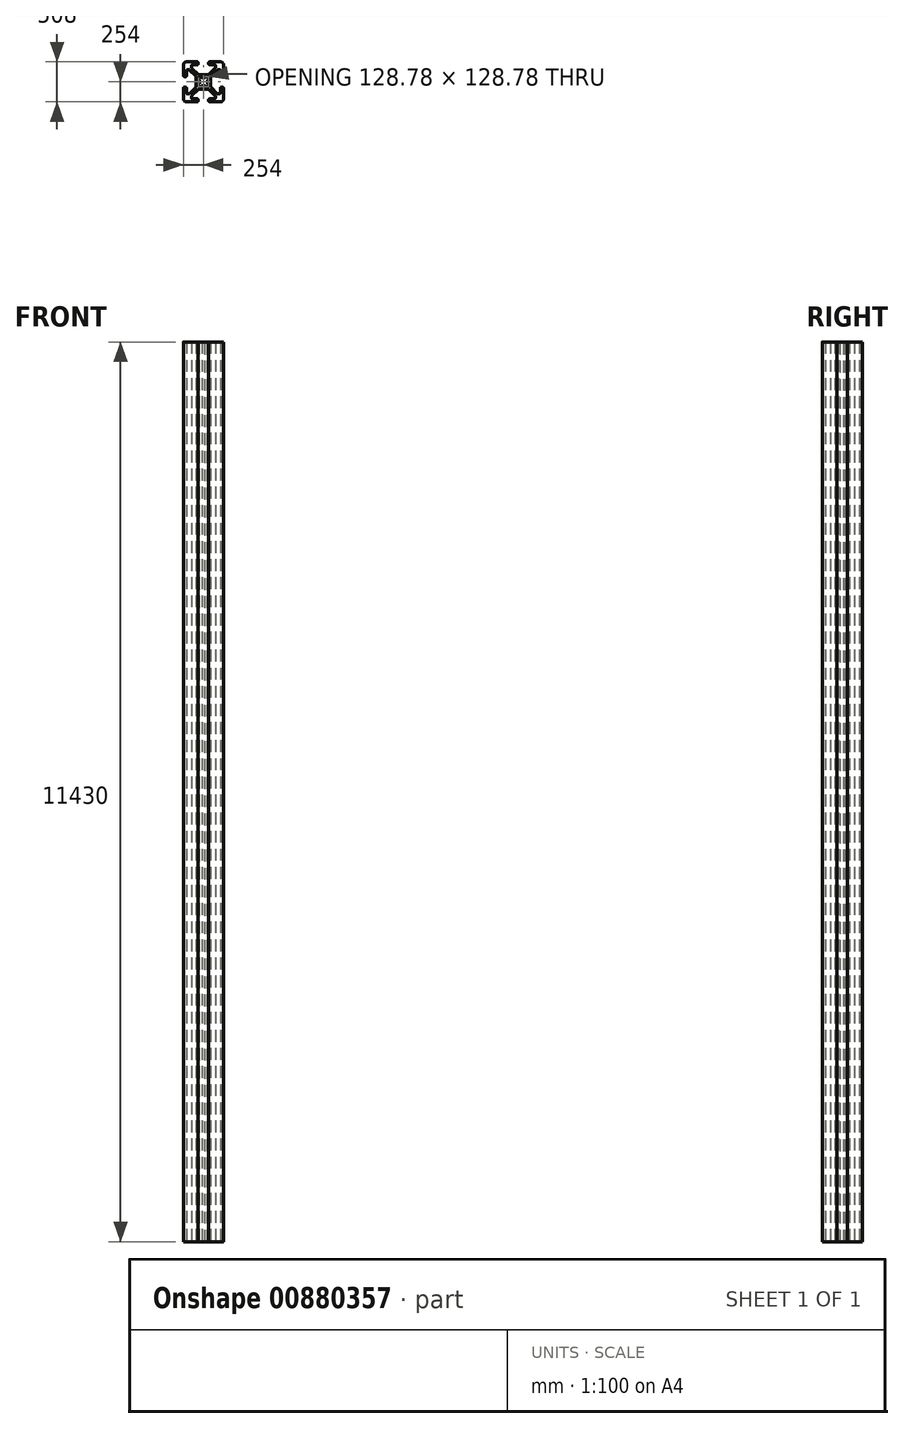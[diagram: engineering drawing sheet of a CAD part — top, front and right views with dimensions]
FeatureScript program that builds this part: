
annotation { "Feature Type Name" : "Feature", "Feature Type Description" : "" }
export const myFeature = defineFeature(function(context is Context, id is Id, definition is map)
    precondition{}
    {
        {
            var Q0;
            Q0=qCreatedBy(makeId("Top.planeOp"),FACE);
            var sketch = newSketch(context, id + "F0", { "sketchPlane" : qUnion([Q0])});
            skArc(sketch, "E0", {"start": v(-53.97, -58.53) * mm, "mid": v(-34.45, -63.65) * mm, "end": v(-20.42, -49.15) * mm});
            skLineSegment(sketch, "E1", {"start": v(-58.53, -53.97) * mm, "end": v(-53.97, -58.53) * mm});
            skArc(sketch, "E2", {"start": v(-49.15, -20.42) * mm, "mid": v(-63.65, -34.45) * mm, "end": v(-58.53, -53.97) * mm});
            skArc(sketch, "E3", {"start": v(-49.15, 20.42) * mm, "mid": v(-53.23, 0) * mm, "end": v(-49.15, -20.42) * mm});
            skArc(sketch, "E4", {"start": v(-58.53, 53.97) * mm, "mid": v(-63.65, 34.45) * mm, "end": v(-49.15, 20.42) * mm});
            skLineSegment(sketch, "E5", {"start": v(-53.97, 58.53) * mm, "end": v(-58.53, 53.97) * mm});
            skArc(sketch, "E6", {"start": v(-20.42, 49.15) * mm, "mid": v(-34.45, 63.65) * mm, "end": v(-53.97, 58.53) * mm});
            skArc(sketch, "E7", {"start": v(20.42, 49.15) * mm, "mid": v(0, 53.23) * mm, "end": v(-20.42, 49.15) * mm});
            skArc(sketch, "E8", {"start": v(53.97, 58.53) * mm, "mid": v(34.45, 63.65) * mm, "end": v(20.42, 49.15) * mm});
            skLineSegment(sketch, "E9", {"start": v(58.53, 53.97) * mm, "end": v(53.97, 58.53) * mm});
            skArc(sketch, "E10", {"start": v(49.15, 20.42) * mm, "mid": v(63.65, 34.45) * mm, "end": v(58.53, 53.97) * mm});
            skArc(sketch, "E11", {"start": v(49.15, -20.42) * mm, "mid": v(53.23, 0) * mm, "end": v(49.15, 20.42) * mm});
            skArc(sketch, "E12", {"start": v(58.53, -53.97) * mm, "mid": v(63.65, -34.45) * mm, "end": v(49.15, -20.42) * mm});
            skLineSegment(sketch, "E13", {"start": v(53.97, -58.53) * mm, "end": v(58.53, -53.97) * mm});
            skArc(sketch, "E14", {"start": v(20.42, -49.15) * mm, "mid": v(34.45, -63.65) * mm, "end": v(53.97, -58.53) * mm});
            skArc(sketch, "E15", {"start": v(-20.42, -49.15) * mm, "mid": v(0, -53.23) * mm, "end": v(20.42, -49.15) * mm});
            skArc(sketch, "E16", {"start": v(241.1, 66.8) * mm, "mid": v(250.22, 70.58) * mm, "end": v(254, 79.7) * mm});
            skLineSegment(sketch, "E17", {"start": v(254, 79.7) * mm, "end": v(254, 215.9) * mm});
            skArc(sketch, "E18", {"start": v(254, 215.9) * mm, "mid": v(242.84, 242.84) * mm, "end": v(215.9, 254) * mm});
            skLineSegment(sketch, "E19", {"start": v(215.9, 254) * mm, "end": v(79.7, 254) * mm});
            skArc(sketch, "E20", {"start": v(79.7, 254) * mm, "mid": v(70.58, 250.22) * mm, "end": v(66.8, 241.1) * mm});
            skLineSegment(sketch, "E21", {"start": v(66.8, 241.1) * mm, "end": v(66.8, 228.8) * mm});
            skArc(sketch, "E22", {"start": v(66.8, 228.8) * mm, "mid": v(70.58, 219.68) * mm, "end": v(79.7, 215.9) * mm});
            skLineSegment(sketch, "E23", {"start": v(79.7, 215.9) * mm, "end": v(139.37, 215.9) * mm});
            skArc(sketch, "E24", {"start": v(152.27, 203) * mm, "mid": v(148.5, 212.12) * mm, "end": v(139.37, 215.9) * mm});
            skLineSegment(sketch, "E25", {"start": v(152.27, 203) * mm, "end": v(152.27, 184.56) * mm});
            skArc(sketch, "E26", {"start": v(148.5, 175.43) * mm, "mid": v(151.3, 179.62) * mm, "end": v(152.27, 184.56) * mm});
            skLineSegment(sketch, "E27", {"start": v(148.5, 175.43) * mm, "end": v(69.68, 96.62) * mm});
            skArc(sketch, "E28", {"start": v(60.55, 92.84) * mm, "mid": v(65.49, 93.82) * mm, "end": v(69.68, 96.62) * mm});
            skLineSegment(sketch, "E29", {"start": v(60.55, 92.84) * mm, "end": v(-60.55, 92.84) * mm});
            skArc(sketch, "E30", {"start": v(-69.68, 96.62) * mm, "mid": v(-65.49, 93.82) * mm, "end": v(-60.55, 92.84) * mm});
            skLineSegment(sketch, "E31", {"start": v(-69.68, 96.62) * mm, "end": v(-148.5, 175.43) * mm});
            skArc(sketch, "E32", {"start": v(-152.27, 184.56) * mm, "mid": v(-151.3, 179.62) * mm, "end": v(-148.5, 175.43) * mm});
            skLineSegment(sketch, "E33", {"start": v(-152.27, 184.56) * mm, "end": v(-152.27, 203) * mm});
            skArc(sketch, "E34", {"start": v(-139.37, 215.9) * mm, "mid": v(-148.5, 212.12) * mm, "end": v(-152.27, 203) * mm});
            skLineSegment(sketch, "E35", {"start": v(-139.37, 215.9) * mm, "end": v(-79.7, 215.9) * mm});
            skArc(sketch, "E36", {"start": v(-79.7, 215.9) * mm, "mid": v(-70.58, 219.68) * mm, "end": v(-66.8, 228.8) * mm});
            skLineSegment(sketch, "E37", {"start": v(-66.8, 228.8) * mm, "end": v(-66.8, 241.1) * mm});
            skArc(sketch, "E38", {"start": v(-66.8, 241.1) * mm, "mid": v(-70.58, 250.22) * mm, "end": v(-79.7, 254) * mm});
            skLineSegment(sketch, "E39", {"start": v(-79.7, 254) * mm, "end": v(-215.9, 254) * mm});
            skArc(sketch, "E40", {"start": v(-215.9, 254) * mm, "mid": v(-242.84, 242.84) * mm, "end": v(-254, 215.9) * mm});
            skLineSegment(sketch, "E41", {"start": v(-254, 215.9) * mm, "end": v(-254, 79.7) * mm});
            skArc(sketch, "E42", {"start": v(-254, 79.7) * mm, "mid": v(-250.22, 70.58) * mm, "end": v(-241.1, 66.8) * mm});
            skLineSegment(sketch, "E43", {"start": v(-241.1, 66.8) * mm, "end": v(-228.8, 66.8) * mm});
            skArc(sketch, "E44", {"start": v(-228.8, 66.8) * mm, "mid": v(-219.68, 70.58) * mm, "end": v(-215.9, 79.7) * mm});
            skLineSegment(sketch, "E45", {"start": v(-215.9, 79.7) * mm, "end": v(-215.9, 139.37) * mm});
            skArc(sketch, "E46", {"start": v(-203, 152.27) * mm, "mid": v(-212.12, 148.5) * mm, "end": v(-215.9, 139.37) * mm});
            skLineSegment(sketch, "E47", {"start": v(-203, 152.27) * mm, "end": v(-184.56, 152.27) * mm});
            skArc(sketch, "E48", {"start": v(-175.43, 148.5) * mm, "mid": v(-179.62, 151.3) * mm, "end": v(-184.56, 152.27) * mm});
            skLineSegment(sketch, "E49", {"start": v(-175.43, 148.5) * mm, "end": v(-96.62, 69.68) * mm});
            skArc(sketch, "E50", {"start": v(-92.84, 60.55) * mm, "mid": v(-93.82, 65.49) * mm, "end": v(-96.62, 69.68) * mm});
            skLineSegment(sketch, "E51", {"start": v(-92.84, 60.55) * mm, "end": v(-92.84, -60.55) * mm});
            skArc(sketch, "E52", {"start": v(-96.62, -69.68) * mm, "mid": v(-93.82, -65.49) * mm, "end": v(-92.84, -60.55) * mm});
            skLineSegment(sketch, "E53", {"start": v(-96.62, -69.68) * mm, "end": v(-175.43, -148.5) * mm});
            skArc(sketch, "E54", {"start": v(-184.56, -152.27) * mm, "mid": v(-179.62, -151.3) * mm, "end": v(-175.43, -148.5) * mm});
            skLineSegment(sketch, "E55", {"start": v(-184.56, -152.27) * mm, "end": v(-203, -152.27) * mm});
            skArc(sketch, "E56", {"start": v(-215.9, -139.37) * mm, "mid": v(-212.12, -148.5) * mm, "end": v(-203, -152.27) * mm});
            skLineSegment(sketch, "E57", {"start": v(-215.9, -139.37) * mm, "end": v(-215.9, -79.7) * mm});
            skArc(sketch, "E58", {"start": v(-215.9, -79.7) * mm, "mid": v(-219.68, -70.58) * mm, "end": v(-228.8, -66.8) * mm});
            skLineSegment(sketch, "E59", {"start": v(-228.8, -66.8) * mm, "end": v(-241.1, -66.8) * mm});
            skArc(sketch, "E60", {"start": v(-241.1, -66.8) * mm, "mid": v(-250.22, -70.58) * mm, "end": v(-254, -79.7) * mm});
            skLineSegment(sketch, "E61", {"start": v(-254, -79.7) * mm, "end": v(-254, -215.9) * mm});
            skArc(sketch, "E62", {"start": v(-254, -215.9) * mm, "mid": v(-242.84, -242.84) * mm, "end": v(-215.9, -254) * mm});
            skLineSegment(sketch, "E63", {"start": v(-215.9, -254) * mm, "end": v(-79.7, -254) * mm});
            skArc(sketch, "E64", {"start": v(-79.7, -254) * mm, "mid": v(-70.58, -250.22) * mm, "end": v(-66.8, -241.1) * mm});
            skLineSegment(sketch, "E65", {"start": v(-66.8, -241.1) * mm, "end": v(-66.8, -228.8) * mm});
            skArc(sketch, "E66", {"start": v(-66.8, -228.8) * mm, "mid": v(-70.58, -219.68) * mm, "end": v(-79.7, -215.9) * mm});
            skLineSegment(sketch, "E67", {"start": v(-79.7, -215.9) * mm, "end": v(-139.37, -215.9) * mm});
            skArc(sketch, "E68", {"start": v(-152.27, -203) * mm, "mid": v(-148.5, -212.12) * mm, "end": v(-139.37, -215.9) * mm});
            skLineSegment(sketch, "E69", {"start": v(-152.27, -203) * mm, "end": v(-152.27, -184.56) * mm});
            skArc(sketch, "E70", {"start": v(-148.5, -175.43) * mm, "mid": v(-151.3, -179.62) * mm, "end": v(-152.27, -184.56) * mm});
            skLineSegment(sketch, "E71", {"start": v(-148.5, -175.43) * mm, "end": v(-69.68, -96.62) * mm});
            skArc(sketch, "E72", {"start": v(-60.55, -92.84) * mm, "mid": v(-65.49, -93.82) * mm, "end": v(-69.68, -96.62) * mm});
            skLineSegment(sketch, "E73", {"start": v(-60.55, -92.84) * mm, "end": v(60.55, -92.84) * mm});
            skArc(sketch, "E74", {"start": v(69.68, -96.62) * mm, "mid": v(65.49, -93.82) * mm, "end": v(60.55, -92.84) * mm});
            skLineSegment(sketch, "E75", {"start": v(69.68, -96.62) * mm, "end": v(148.5, -175.43) * mm});
            skArc(sketch, "E76", {"start": v(152.27, -184.56) * mm, "mid": v(151.3, -179.62) * mm, "end": v(148.5, -175.43) * mm});
            skLineSegment(sketch, "E77", {"start": v(152.27, -184.56) * mm, "end": v(152.27, -203) * mm});
            skArc(sketch, "E78", {"start": v(139.37, -215.9) * mm, "mid": v(148.5, -212.12) * mm, "end": v(152.27, -203) * mm});
            skLineSegment(sketch, "E79", {"start": v(139.37, -215.9) * mm, "end": v(79.7, -215.9) * mm});
            skArc(sketch, "E80", {"start": v(79.7, -215.9) * mm, "mid": v(70.58, -219.68) * mm, "end": v(66.8, -228.8) * mm});
            skLineSegment(sketch, "E81", {"start": v(66.8, -228.8) * mm, "end": v(66.8, -241.1) * mm});
            skArc(sketch, "E82", {"start": v(66.8, -241.1) * mm, "mid": v(70.58, -250.22) * mm, "end": v(79.7, -254) * mm});
            skLineSegment(sketch, "E83", {"start": v(79.7, -254) * mm, "end": v(215.9, -254) * mm});
            skArc(sketch, "E84", {"start": v(215.9, -254) * mm, "mid": v(242.84, -242.84) * mm, "end": v(254, -215.9) * mm});
            skLineSegment(sketch, "E85", {"start": v(254, -215.9) * mm, "end": v(254, -79.7) * mm});
            skArc(sketch, "E86", {"start": v(254, -79.7) * mm, "mid": v(250.22, -70.58) * mm, "end": v(241.1, -66.8) * mm});
            skLineSegment(sketch, "E87", {"start": v(241.1, -66.8) * mm, "end": v(228.8, -66.8) * mm});
            skArc(sketch, "E88", {"start": v(228.8, -66.8) * mm, "mid": v(219.68, -70.58) * mm, "end": v(215.9, -79.7) * mm});
            skLineSegment(sketch, "E89", {"start": v(215.9, -79.7) * mm, "end": v(215.9, -139.37) * mm});
            skArc(sketch, "E90", {"start": v(203, -152.27) * mm, "mid": v(212.12, -148.5) * mm, "end": v(215.9, -139.37) * mm});
            skLineSegment(sketch, "E91", {"start": v(203, -152.27) * mm, "end": v(184.56, -152.27) * mm});
            skArc(sketch, "E92", {"start": v(175.43, -148.5) * mm, "mid": v(179.62, -151.3) * mm, "end": v(184.56, -152.27) * mm});
            skLineSegment(sketch, "E93", {"start": v(175.43, -148.5) * mm, "end": v(96.62, -69.68) * mm});
            skArc(sketch, "E94", {"start": v(92.84, -60.55) * mm, "mid": v(93.82, -65.49) * mm, "end": v(96.62, -69.68) * mm});
            skLineSegment(sketch, "E95", {"start": v(92.84, -60.55) * mm, "end": v(92.84, 60.55) * mm});
            skArc(sketch, "E96", {"start": v(96.62, 69.68) * mm, "mid": v(93.82, 65.49) * mm, "end": v(92.84, 60.55) * mm});
            skLineSegment(sketch, "E97", {"start": v(96.62, 69.68) * mm, "end": v(175.43, 148.5) * mm});
            skArc(sketch, "E98", {"start": v(184.56, 152.27) * mm, "mid": v(179.62, 151.3) * mm, "end": v(175.43, 148.5) * mm});
            skLineSegment(sketch, "E99", {"start": v(184.56, 152.27) * mm, "end": v(203, 152.27) * mm});
            skArc(sketch, "E100", {"start": v(215.9, 139.37) * mm, "mid": v(212.12, 148.5) * mm, "end": v(203, 152.27) * mm});
            skLineSegment(sketch, "E101", {"start": v(215.9, 139.37) * mm, "end": v(215.9, 79.7) * mm});
            skArc(sketch, "E102", {"start": v(215.9, 79.7) * mm, "mid": v(219.68, 70.58) * mm, "end": v(228.8, 66.8) * mm});
            skLineSegment(sketch, "E103", {"start": v(228.8, 66.8) * mm, "end": v(241.1, 66.8) * mm});
            skSolve(sketch);
        }
        {
            var Q0;
            Q0=makeQuery(id+"F0.imprint","IMPRINT",FACE,{"disambiguationData":[TD([[makeQuery(id+"F0.imprint","IMPRINT",EDGE,{"derivedFrom":sQuery(id+"F0.wireOp",EDGE,"E0")}),-1.0]])]});
            extrude(context, id + "F1", {"entities" : qUnion([Q0]), "depth" : 11430 * mm, "offsetDistance" : 25.4 * mm});
        }
    });
